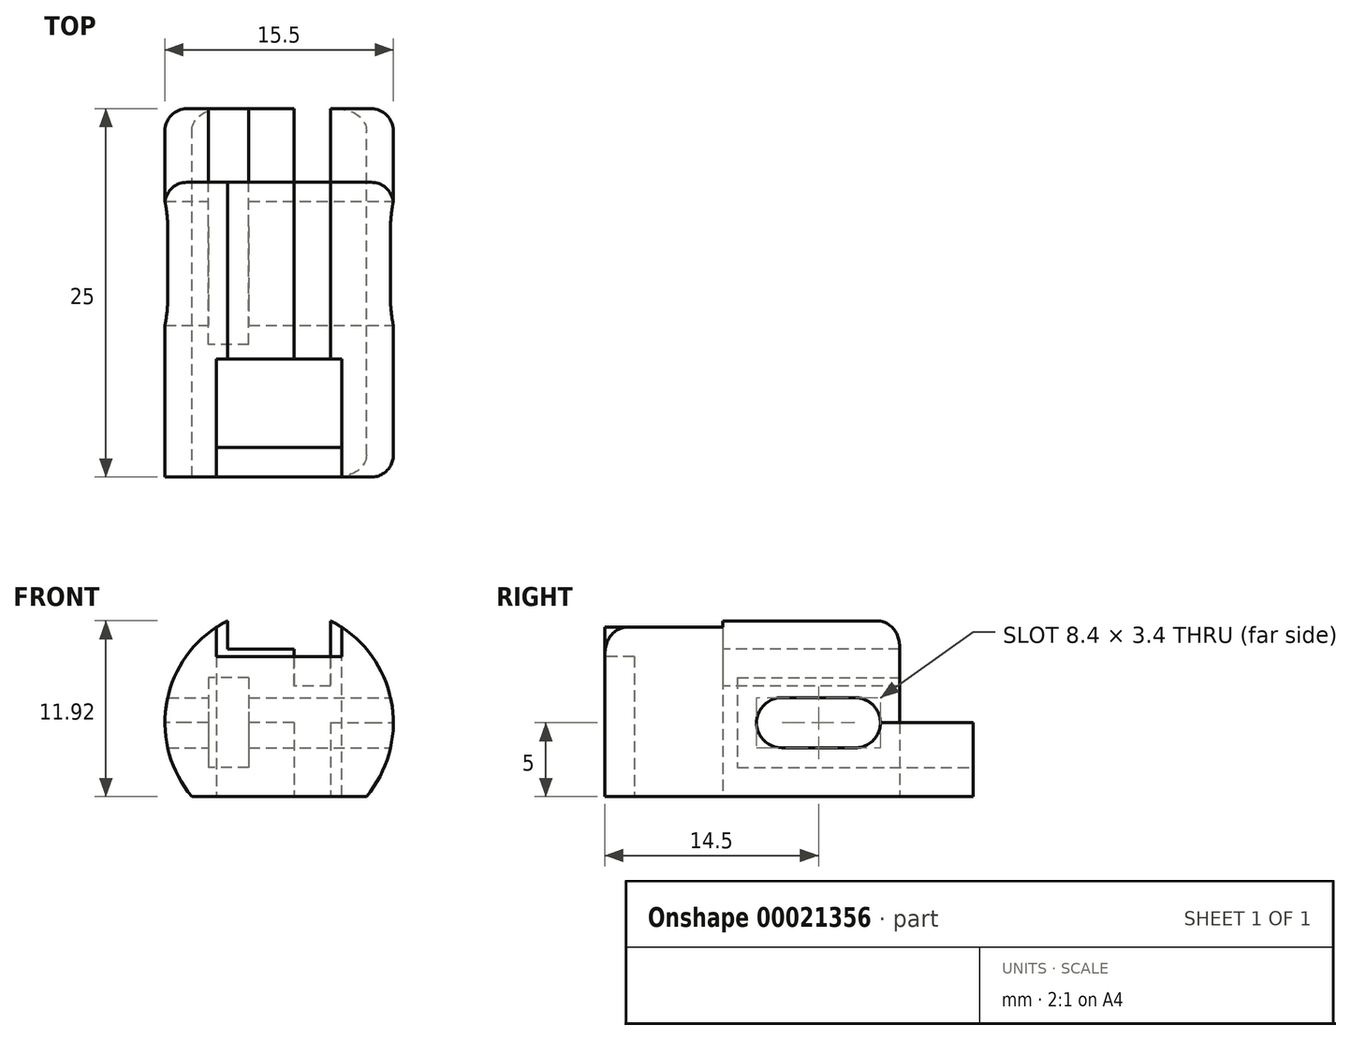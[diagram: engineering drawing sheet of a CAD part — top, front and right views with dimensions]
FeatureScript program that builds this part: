
annotation { "Feature Type Name" : "Feature", "Feature Type Description" : "" }
export const myFeature = defineFeature(function(context is Context, id is Id, definition is map)
    precondition{}
    {
        {
            var Q0;
            Q0=qCreatedBy(makeId("Front.planeOp"),FACE);
            var sketch = newSketch(context, id + "F0", { "sketchPlane" : qUnion([Q0])});
            skArc(sketch, "E0", {"start": v(-3.5, 6.91) * mm, "mid": v(-7.6, 1.54) * mm, "end": v(-5.92, -5) * mm});
            skArc(sketch, "E1", {"start": v(5.92, -5) * mm, "mid": v(7.6, 1.54) * mm, "end": v(3.5, 6.91) * mm});
            skLineSegment(sketch, "E2", {"start": v(-5.92, -5) * mm, "end": v(5.92, -5) * mm});
            skLineSegment(sketch, "E3", {"start": v(-3.5, 6.91) * mm, "end": v(3.5, 6.91) * mm});
            skSolve(sketch);
        }
        {
            var Q0;
            Q0 = qSketchRegion(id + "F0", true);
            extrude(context, id + "F1", {"entities" : qUnion([Q0]), "depth" : 20 * mm});
        }
        {
            var Q0;
            Q0=makeQuery(id+"F1.opExtrude","CAP_FACE",FACE,{"disambiguationData":[OSD([sQuery(id+"F0.wireOp",EDGE,"E0"),sQuery(id+"F0.wireOp",EDGE,"E1"),sQuery(id+"F0.wireOp",EDGE,"E2"),sQuery(id+"F0.wireOp",EDGE,"E3")])],"isStart":false});
            var sketch = newSketch(context, id + "F2", { "sketchPlane" : qUnion([Q0])});
            skLineSegment(sketch, "E4", {"start": v(-4.25, 6.48) * mm, "end": v(-4.25, 4.5) * mm});
            skLineSegment(sketch, "E5", {"start": v(-4.25, 4.5) * mm, "end": v(4.25, 4.5) * mm});
            skLineSegment(sketch, "E6", {"start": v(4.25, 4.5) * mm, "end": v(4.25, 6.48) * mm});
            skSolve(sketch);
        }
        {
            var Q0;
            {var subQ4=sQuery(id+"F2.wireOp",EDGE,"E4");Q0=makeQuery(id+"F2.imprint","IMPRINT",FACE,{"disambiguationData":[TD([[makeQuery(id+"F2.imprint","IMPRINT",EDGE,{"derivedFrom":subQ4}),1.0]])]});}
            extrude(context, id + "F3", {"entities" : qUnion([Q0]), "operationType" : NewBodyOperationType.REMOVE, "oppositeDirection" : true, "depth" : 2 * mm});
        }
        {
            var Q0;
            Q0=makeQuery(id+"F3.boolean.opBoolean","COPY",FACE,{"derivedFrom":makeQuery(id+"F3.opExtrude","CAP_FACE",FACE,{"disambiguationData":[OSD([sQuery(id+"F0.wireOp",EDGE,"E0"),sQuery(id+"F0.wireOp",EDGE,"E1"),sQuery(id+"F0.wireOp",EDGE,"E3"),sQuery(id+"F2.wireOp",EDGE,"E4"),sQuery(id+"F2.wireOp",EDGE,"E5"),sQuery(id+"F2.wireOp",EDGE,"E6")])],"isStart":false})});
            var sketch = newSketch(context, id + "F4", { "sketchPlane" : qUnion([Q0])});
            skLineSegment(sketch, "E7.0", {"start": v(-4.25, 6.48) * mm, "end": v(-4.25, 4.5) * mm});
            skLineSegment(sketch, "E8.0", {"start": v(4.25, 4.5) * mm, "end": v(4.25, 6.48) * mm});
            skLineSegment(sketch, "E9.0", {"start": v(-5.92, -5) * mm, "end": v(5.92, -5) * mm});
            skLineSegment(sketch, "E10", {"start": v(-4.25, 4.5) * mm, "end": v(-4.25, -5) * mm});
            skLineSegment(sketch, "E11", {"start": v(4.25, 4.5) * mm, "end": v(4.25, -5) * mm});
            skSolve(sketch);
        }
        {
            var Q0;
            Q0=makeQuery(id+"F4.imprint","IMPRINT",FACE,{"disambiguationData":[TD([[makeQuery(id+"F4.imprint","IMPRINT",EDGE,{"derivedFrom":sQuery(id+"F4.wireOp",EDGE,"E7.0")}),1.0]])]});
            var Q1;
            {var subQ1=sQuery(id+"F4.wireOp",EDGE,"E10");Q1=makeQuery(id+"F4.imprint","IMPRINT",FACE,{"disambiguationData":[TD([[makeQuery(id+"F4.imprint","IMPRINT",EDGE,{"derivedFrom":subQ1}),1.0]])]});}
            extrude(context, id + "F5", {"entities" : qUnion([Q0, Q1]), "operationType" : NewBodyOperationType.REMOVE, "oppositeDirection" : true, "depth" : 6 * mm});
        }
        {
            var Q0;
            Q0=makeQuery(id+"F5.boolean.opBoolean","COPY",FACE,{"derivedFrom":makeQuery(id+"F5.opExtrude","CAP_FACE",FACE,{"disambiguationData":[OSD([sQuery(id+"F0.wireOp",EDGE,"E0"),sQuery(id+"F0.wireOp",EDGE,"E1"),sQuery(id+"F0.wireOp",EDGE,"E3"),sQuery(id+"F4.wireOp",EDGE,"E7.0"),sQuery(id+"F4.wireOp",EDGE,"E8.0"),sQuery(id+"F4.wireOp",EDGE,"E9.0"),sQuery(id+"F4.wireOp",EDGE,"E10"),sQuery(id+"F4.wireOp",EDGE,"E11")])],"isStart":false})});
            var sketch = newSketch(context, id + "F6", { "sketchPlane" : qUnion([Q0])});
            skLineSegment(sketch, "E12", {"start": v(-3.5, 6.91) * mm, "end": v(-3.5, 5) * mm});
            skLineSegment(sketch, "E13", {"start": v(-3.5, 5) * mm, "end": v(1, 5) * mm});
            skLineSegment(sketch, "E14", {"start": v(1, 5) * mm, "end": v(1, 2.5) * mm});
            skLineSegment(sketch, "E15", {"start": v(1, 2.5) * mm, "end": v(3.5, 2.5) * mm});
            skLineSegment(sketch, "E16", {"start": v(3.5, 6.91) * mm, "end": v(3.5, 2.5) * mm});
            skSolve(sketch);
        }
        {
            var Q0;
            Q0=makeQuery(id+"F6.imprint","IMPRINT",FACE,{"disambiguationData":[TD([[makeQuery(id+"F6.imprint","IMPRINT",EDGE,{"derivedFrom":sQuery(id+"F6.wireOp",EDGE,"E12")}),1.0]])]});
            extrude(context, id + "F7", {"entities" : qUnion([Q0]), "operationType" : NewBodyOperationType.REMOVE, "endBound" : BoundingType.UP_TO_NEXT, "oppositeDirection" : true, "depth" : 25 * mm});
        }
        {
            var Q0;
            Q0=qCreatedBy(makeId("Right.planeOp"),FACE);
            var sketch = newSketch(context, id + "F8", { "sketchPlane" : qUnion([Q0])});
            skArc(sketch, "E17", {"start": v(-8, 1.7) * mm, "mid": v(-9.7, 0) * mm, "end": v(-8, -1.7) * mm});
            skLineSegment(sketch, "E18", {"start": v(-8, 1.7) * mm, "end": v(-8, -1.7) * mm, "construction": true});
            skLineSegment(sketch, "E19", {"start": v(-8, 1.7) * mm, "end": v(-3, 1.7) * mm});
            skLineSegment(sketch, "E20", {"start": v(-8, -1.7) * mm, "end": v(-3, -1.7) * mm});
            skLineSegment(sketch, "E21", {"start": v(-3, 1.7) * mm, "end": v(-3, -1.7) * mm, "construction": true});
            skArc(sketch, "E22", {"start": v(-3, -1.7) * mm, "mid": v(-1.3, 0) * mm, "end": v(-3, 1.7) * mm});
            skSolve(sketch);
        }
        {
            var Q0;
            Q0 = qSketchRegion(id + "F8", true);
            extrude(context, id + "F9", {"entities" : qUnion([Q0]), "operationType" : NewBodyOperationType.REMOVE, "endBound" : BoundingType.SYMMETRIC, "oppositeDirection" : true, "depth" : 25 * mm});
        }
        {
            var Q0;
            Q0=makeQuery(id+"F1.opExtrude","CAP_FACE",FACE,{"disambiguationData":[OSD([sQuery(id+"F0.wireOp",EDGE,"E0"),sQuery(id+"F0.wireOp",EDGE,"E1"),sQuery(id+"F0.wireOp",EDGE,"E2"),sQuery(id+"F0.wireOp",EDGE,"E3")])],"isStart":true});
            var sketch = newSketch(context, id + "F10", { "sketchPlane" : qUnion([Q0])});
            skLineSegment(sketch, "E23.bottom", {"start": v(2.05, 3.05) * mm, "end": v(4.8, 3.05) * mm});
            skLineSegment(sketch, "E23.top", {"start": v(2.05, -3.05) * mm, "end": v(4.8, -3.05) * mm});
            skLineSegment(sketch, "E23.left", {"start": v(2.05, 3.05) * mm, "end": v(2.05, -3.05) * mm});
            skLineSegment(sketch, "E23.right", {"start": v(4.8, 3.05) * mm, "end": v(4.8, -3.05) * mm});
            skSolve(sketch);
        }
        {
            var Q0;
            Q0 = qSketchRegion(id + "F10", true);
            extrude(context, id + "F11", {"entities" : qUnion([Q0]), "operationType" : NewBodyOperationType.REMOVE, "oppositeDirection" : true, "depth" : 11 * mm});
        }
        {
            var Q0;
            Q0=makeQuery(id+"F1.opExtrude","CAP_FACE",FACE,{"disambiguationData":[OSD([sQuery(id+"F0.wireOp",EDGE,"E0"),sQuery(id+"F0.wireOp",EDGE,"E1"),sQuery(id+"F0.wireOp",EDGE,"E2"),sQuery(id+"F0.wireOp",EDGE,"E3")])],"isStart":true});
            var sketch = newSketch(context, id + "F12", { "sketchPlane" : qUnion([Q0])});
            skLineSegment(sketch, "E24", {"start": v(-3.5, 2.5) * mm, "end": v(-3.5, -5) * mm});
            skLineSegment(sketch, "E25", {"start": v(-3.5, 0) * mm, "end": v(-7.75, 0) * mm});
            skLineSegment(sketch, "E26", {"start": v(-1, 2.5) * mm, "end": v(-1, -5) * mm});
            skLineSegment(sketch, "E27", {"start": v(-1, 0) * mm, "end": v(2.05, 0) * mm});
            skLineSegment(sketch, "E28", {"start": v(4.8, 0) * mm, "end": v(7.75, 0) * mm});
            skSolve(sketch);
        }
        {
            var Q0;
            {var subQ5=sQuery(id+"F12.wireOp",EDGE,"E25");Q0=makeQuery(id+"F12.imprint","IMPRINT",FACE,{"disambiguationData":[TD([[makeQuery(id+"F12.imprint","IMPRINT",EDGE,{"derivedFrom":subQ5}),1.0]])]});}
            var Q1;
            {var subQ4=sQuery(id+"F12.wireOp",EDGE,"E27");Q1=makeQuery(id+"F12.imprint","IMPRINT",FACE,{"disambiguationData":[TD([[makeQuery(id+"F12.imprint","IMPRINT",EDGE,{"derivedFrom":subQ4}),-1.0]])]});}
            extrude(context, id + "F13", {"entities" : qUnion([Q0, Q1]), "operationType" : NewBodyOperationType.ADD, "depth" : 5 * mm});
        }
        {
            var Q0;
            Q0=makeQuery(id+"F1.opExtrude","CAP_EDGE",EDGE,{"disambiguationData":[OSD([sQuery(id+"F0.wireOp",EDGE,"E1")])],"isStart":false});
            var Q1;
            Q1=makeQuery(id+"F1.opExtrude","CAP_EDGE",EDGE,{"disambiguationData":[OSD([sQuery(id+"F0.wireOp",EDGE,"E1")])],"isStart":true});
            var Q2;
            Q2=makeQuery(id+"F13.opExtrude","CAP_EDGE",EDGE,{"disambiguationData":[OSD([sQuery(id+"F0.wireOp",EDGE,"E1")])],"isStart":false});
            var Q3;
            Q3=makeQuery(id+"F13.opExtrude","CAP_EDGE",EDGE,{"disambiguationData":[OSD([sQuery(id+"F0.wireOp",EDGE,"E0")])],"isStart":false});
            var Q4;
            Q4=makeQuery(id+"F1.opExtrude","CAP_EDGE",EDGE,{"disambiguationData":[OSD([sQuery(id+"F0.wireOp",EDGE,"E0")])],"isStart":true});
            fillet(context, id + "F14", {"entities" : qUnion([Q0, Q1, Q2, Q3, Q4]), "radius" : 1.5 * mm, "tangentPropagation" : true, "allowEdgeOverflow" : false});
        }
    });
